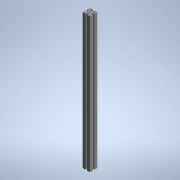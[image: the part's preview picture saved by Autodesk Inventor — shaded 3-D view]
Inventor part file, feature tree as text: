
AUTODESK INVENTOR PART (.ipt)
format: ipt  version: 2022 (Build 260153000, 153)  size: 223,744 bytes
history: native  units: mm (DEFAULTED — no unit token found)
features: other x21, sketch x2, extrude x1, hole x1
ambient origin geometry x8: Origin, YZ Plane, XZ Plane, XY Plane, X Axis, Y Axis, Z Axis, Center Point
bodies: Solid1 (feature_tree)
feature tree (25):
  extrude  "Extrusion1"  TaperAngle=0.0deg  [1 undecoded]
  hole  "Hole1"  [1 undecoded]
  other  "C1_XY"
  other  "C1_YZ"
  other  "C1_ZX"
  other  "C1_X"
  other  "C1_Y"
  other  "C1_Z"
  other  "C1_Center"
  other  "to_frame_cap1_XY"
  other  "to_frame_cap1_YZ"
  other  "to_frame_cap1_ZX"
  other  "to_frame_cap1_X"
  other  "to_frame_cap1_Y"
  other  "to_frame_cap1_Z"
  other  "to_frame_cap1_Center"
  other  "to_frame_cap2_XY"
  other  "to_frame_cap2_YZ"
  other  "to_frame_cap2_ZX"
  other  "to_frame_cap2_X"
  other  "to_frame_cap2_Y"
  other  "to_frame_cap2_Z"
  other  "to_frame_cap2_Center"
  sketch  "Sketch_60"  dims[d2=10.5mm d3=6.0mm d4=4.0mm d5=2.0mm d6=90.0deg d7=1000.0mm d8=0.0mm d9=0.0mm d10=0.0mm d11=0.0mm d12=152.4mm d13=0.872665mm d14=152.4mm d15=0.872665mm]
  sketch  "Sketch2"  dims[d0=1066.8mm d1=0.0mm]
note: 2 required parameter values undecoded (feature->parameter linkage not recoverable at this tier; creation-order binding heuristic only, values carry confidence <= 0.55)
